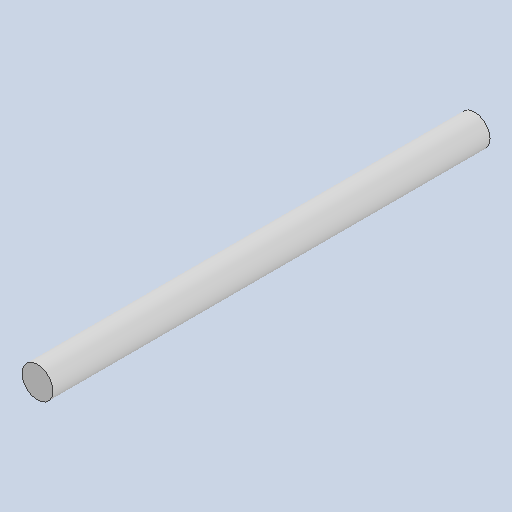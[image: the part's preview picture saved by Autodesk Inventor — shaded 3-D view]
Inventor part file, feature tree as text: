
AUTODESK INVENTOR PART (.ipt)
format: ipt  version: 2024.1 (Build 281209000, 209)  size: 86,016 bytes
history: native  units: mm
features: sketch x2, extrude x1
ambient origin geometry x8: Origin, YZ Plane, XZ Plane, XY Plane, X Axis, Y Axis, Z Axis, Center Point
bodies: Solid1 (feature_tree)
feature tree (3):
  sketch  "Sketch1"  dims[d0=4.25mm d1=60.0mm d2=0.0mm]
  extrude  "Extrusion1"  Depth=60.0mm TaperAngle=0.0deg
  sketch  "Sketch2"
